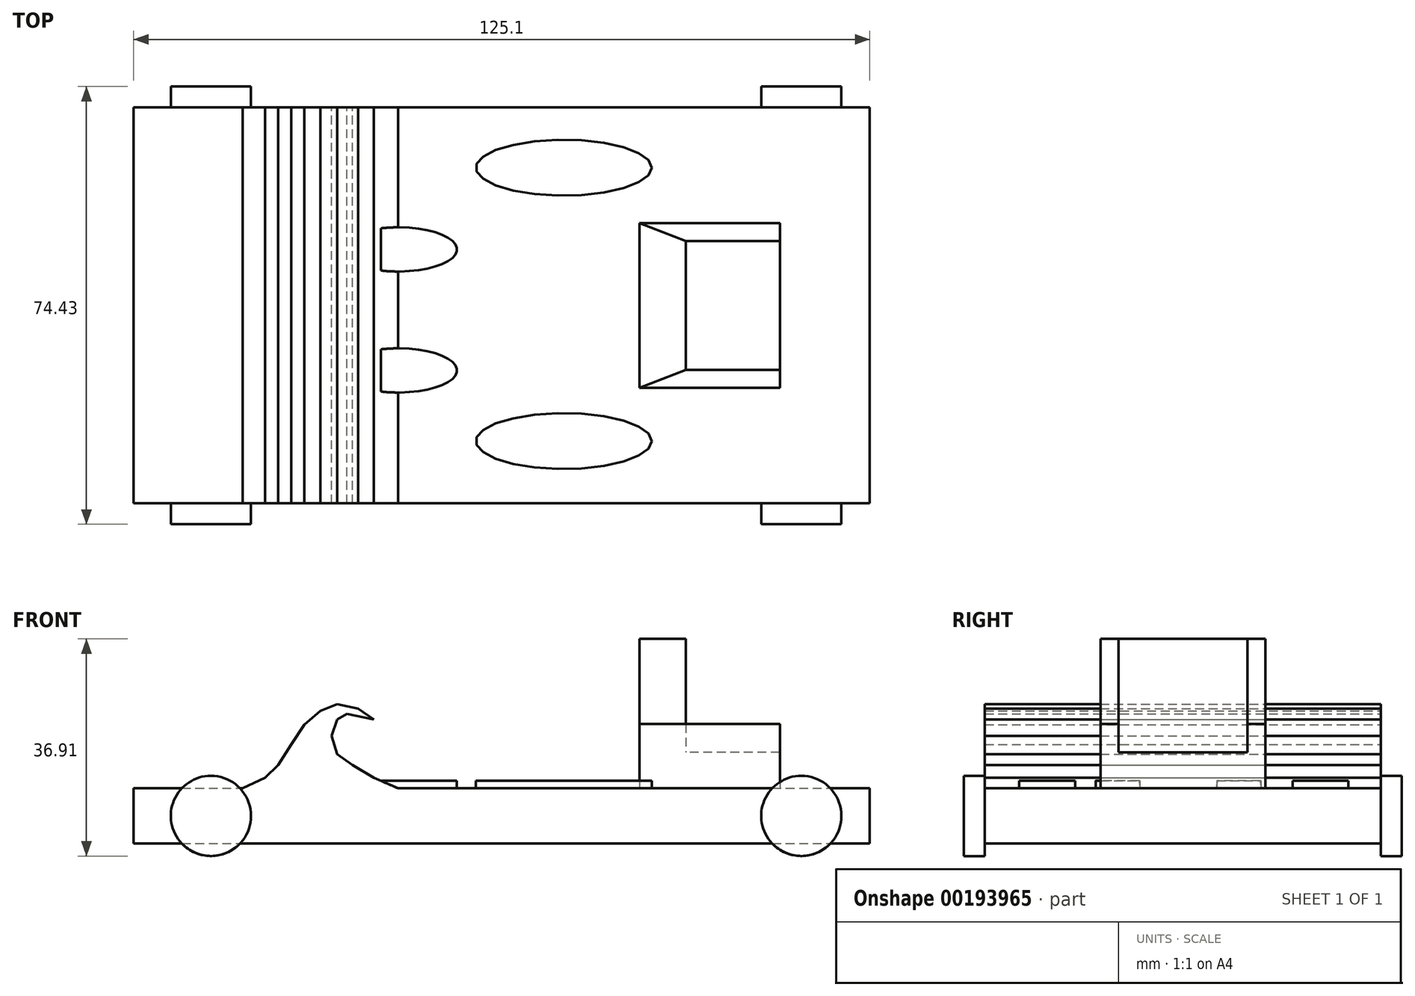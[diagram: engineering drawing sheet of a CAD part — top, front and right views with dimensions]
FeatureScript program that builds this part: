
annotation { "Feature Type Name" : "Feature", "Feature Type Description" : "" }
export const myFeature = defineFeature(function(context is Context, id is Id, definition is map)
    precondition{}
    {
        {
            var Q0;
            Q0=qCreatedBy(makeId("Front.planeOp"),FACE);
            var sketch = newSketch(context, id + "F0", { "sketchPlane" : qUnion([Q0])});
            skLineSegment(sketch, "E0.bottom", {"start": v(-59.68, 0) * mm, "end": v(65.42, 0) * mm});
            skLineSegment(sketch, "E0.top", {"start": v(-59.68, 9.38) * mm, "end": v(65.42, 9.38) * mm});
            skLineSegment(sketch, "E0.left", {"start": v(-59.68, 0) * mm, "end": v(-59.68, 9.38) * mm});
            skLineSegment(sketch, "E0.right", {"start": v(65.42, 0) * mm, "end": v(65.42, 9.38) * mm});
            skLineSegment(sketch, "E1", {"start": v(-41.18, 9.38) * mm, "end": v(-37.35, 11.18) * mm});
            skLineSegment(sketch, "E2", {"start": v(-37.35, 11.18) * mm, "end": v(-35.09, 13.35) * mm});
            skLineSegment(sketch, "E3", {"start": v(-35.09, 13.35) * mm, "end": v(-32.91, 16.83) * mm});
            skLineSegment(sketch, "E4", {"start": v(-32.91, 16.83) * mm, "end": v(-30.65, 20.23) * mm});
            skLineSegment(sketch, "E5", {"start": v(-30.65, 20.23) * mm, "end": v(-27.96, 22.57) * mm});
            skLineSegment(sketch, "E6", {"start": v(-27.96, 22.57) * mm, "end": v(-25.09, 23.7) * mm});
            skLineSegment(sketch, "E7", {"start": v(-25.09, 23.7) * mm, "end": v(-21.52, 22.92) * mm});
            skLineSegment(sketch, "E8", {"start": v(-21.52, 22.92) * mm, "end": v(-18.82, 21.1) * mm});
            skLineSegment(sketch, "E9", {"start": v(-18.82, 21.1) * mm, "end": v(-23.43, 22.05) * mm});
            skLineSegment(sketch, "E10", {"start": v(-23.43, 22.05) * mm, "end": v(-25.09, 21.1) * mm});
            skLineSegment(sketch, "E11", {"start": v(-25.09, 21.1) * mm, "end": v(-26.04, 18.31) * mm});
            skLineSegment(sketch, "E12", {"start": v(-26.04, 18.31) * mm, "end": v(-25.09, 15.18) * mm});
            skLineSegment(sketch, "E13", {"start": v(-25.09, 15.18) * mm, "end": v(-22.48, 13.35) * mm});
            skLineSegment(sketch, "E14", {"start": v(-22.48, 13.35) * mm, "end": v(-18.82, 11.18) * mm});
            skLineSegment(sketch, "E15", {"start": v(-18.82, 11.18) * mm, "end": v(-14.74, 9.38) * mm});
            skSolve(sketch);
        }
        {
            var Q0;
            Q0=makeQuery(id+"F0.imprint","IMPRINT",FACE,{"disambiguationData":[TD([[makeQuery(id+"F0.imprint","IMPRINT",EDGE,{"derivedFrom":sQuery(id+"F0.wireOp",EDGE,"E0.bottom")}),1.0]])]});
            var Q1;
            {var subQ0=sQuery(id+"F0.wireOp",EDGE,"E1");Q1=makeQuery(id+"F0.imprint","IMPRINT",FACE,{"disambiguationData":[TD([[makeQuery(id+"F0.imprint","IMPRINT",EDGE,{"derivedFrom":subQ0}),-1.0]])]});}
            extrude(context, id + "F1", {"entities" : qUnion([Q0, Q1]), "depth" : 67.3 * mm});
        }
        {
            var Q0;
            {var subQ0=sQuery(id+"F0.wireOp",EDGE,"E0.top");Q0=makeQuery(id+"F1.opExtrude","SWEPT_FACE",FACE,{"disambiguationData":[OSD([subQ0]),TDD([makeQuery(id+"F0.imprint","IMPRINT",EDGE,{"disambiguationData":[TD([[makeQuery(id+"F0.imprint","INTERSECT",VERTEX,{"derivedFrom":[subQ0,sQuery(id+"F0.wireOp",EDGE,"E0.right")]}),1.0]])],"derivedFrom":subQ0})])]});}
            var sketch = newSketch(context, id + "F2", { "sketchPlane" : qUnion([Q0])});
            skEllipse(sketch, "E16", {"center": v(13.42, -56.73) * mm, "majorRadius": 14.94 * mm, "minorRadius": 4.74 * mm, "majorAxis": v(1, 0)});
            skEllipse(sketch, "E17.0.1.0", {"center": v(13.42, -41.23) * mm, "majorRadius": 14.94 * mm, "minorRadius": 4.74 * mm, "majorAxis": v(1, 0)});
            skEllipse(sketch, "E17.0.2.0", {"center": v(13.42, -25.74) * mm, "majorRadius": 14.94 * mm, "minorRadius": 4.74 * mm, "majorAxis": v(1, 0)});
            skEllipse(sketch, "E17.0.3.0", {"center": v(13.42, -10.25) * mm, "majorRadius": 14.94 * mm, "minorRadius": 4.74 * mm, "majorAxis": v(1, 0)});
            skLineSegment(sketch, "E17.direction1", {"start": v(13.42, -56.73) * mm, "end": v(24.6, -56.73) * mm, "construction": true});
            skLineSegment(sketch, "E17.direction2", {"start": v(13.42, -56.73) * mm, "end": v(13.42, -41.23) * mm, "construction": true});
            skSolve(sketch);
        }
        {
            var Q0;
            Q0=makeQuery(id+"F2.imprint","IMPRINT",FACE,{"disambiguationData":[TD([[makeQuery(id+"F2.imprint","IMPRINT",EDGE,{"derivedFrom":sQuery(id+"F2.wireOp",EDGE,"E16")}),1.0]])]});
            var Q1;
            Q1=makeQuery(id+"F2.imprint","IMPRINT",FACE,{"disambiguationData":[TD([[makeQuery(id+"F2.imprint","IMPRINT",EDGE,{"derivedFrom":sQuery(id+"F2.wireOp",EDGE,"E17.0.3.0")}),1.0]])]});
            extrude(context, id + "F3", {"entities" : qUnion([Q0, Q1]), "operationType" : NewBodyOperationType.ADD, "depth" : 1.27 * mm});
        }
        {
            var Q0;
            {var subQ0=sQuery(id+"F0.wireOp",EDGE,"E0.top");Q0=makeQuery(id+"F1.opExtrude","SWEPT_FACE",FACE,{"disambiguationData":[OSD([subQ0]),TDD([makeQuery(id+"F0.imprint","IMPRINT",EDGE,{"disambiguationData":[TD([[makeQuery(id+"F0.imprint","INTERSECT",VERTEX,{"derivedFrom":[subQ0,sQuery(id+"F0.wireOp",EDGE,"E0.right")]}),1.0]])],"derivedFrom":subQ0})])]});}
            var sketch = newSketch(context, id + "F4", { "sketchPlane" : qUnion([Q0])});
            skEllipse(sketch, "E18", {"center": v(-14.74, -44.72) * mm, "majorRadius": 10 * mm, "minorRadius": 3.76 * mm, "majorAxis": v(-1, 0)});
            skEllipse(sketch, "E19.0.1.0", {"center": v(-14.74, -24.15) * mm, "majorRadius": 10 * mm, "minorRadius": 3.76 * mm, "majorAxis": v(-1, 0)});
            skLineSegment(sketch, "E19.direction1", {"start": v(-14.74, -44.72) * mm, "end": v(10.66, -44.72) * mm, "construction": true});
            skLineSegment(sketch, "E19.direction2", {"start": v(-14.74, -44.72) * mm, "end": v(-14.74, -24.15) * mm, "construction": true});
            skSolve(sketch);
        }
        {
            var Q0;
            Q0 = qSketchRegion(id + "F4", true);
            extrude(context, id + "F5", {"entities" : qUnion([Q0]), "operationType" : NewBodyOperationType.ADD, "depth" : 1.27 * mm});
        }
        {
            var Q0;
            {var subQ0=sQuery(id+"F0.wireOp",EDGE,"E0.top");Q0=makeQuery(id+"F1.opExtrude","SWEPT_FACE",FACE,{"disambiguationData":[OSD([subQ0]),TDD([makeQuery(id+"F0.imprint","IMPRINT",EDGE,{"disambiguationData":[TD([[makeQuery(id+"F0.imprint","INTERSECT",VERTEX,{"derivedFrom":[subQ0,sQuery(id+"F0.wireOp",EDGE,"E0.right")]}),1.0]])],"derivedFrom":subQ0})])]});}
            var sketch = newSketch(context, id + "F6", { "sketchPlane" : qUnion([Q0])});
            skLineSegment(sketch, "E20.bottom", {"start": v(50.14, -22.7) * mm, "end": v(34.16, -22.7) * mm});
            skLineSegment(sketch, "E20.top", {"start": v(50.14, -44.61) * mm, "end": v(34.16, -44.61) * mm});
            skLineSegment(sketch, "E20.left", {"start": v(50.14, -22.7) * mm, "end": v(50.14, -44.61) * mm});
            skLineSegment(sketch, "E20.right", {"start": v(34.16, -22.7) * mm, "end": v(34.16, -44.61) * mm});
            skPoint(sketch, "E20.middle", {"position": v(42.15, -33.65) * mm});
            skPoint(sketch, "E20.middle.positionSnap0", {"position": v(65.42, -33.65) * mm});
            skPoint(sketch, "E20.centerSnap0", {"position": v(65.42, -33.65) * mm});
            skLineSegment(sketch, "E21", {"start": v(42.15, -33.65) * mm, "end": v(26.31, -33.65) * mm, "construction": true});
            skLineSegment(sketch, "E22", {"start": v(34.16, -44.61) * mm, "end": v(26.31, -47.66) * mm});
            skLineSegment(sketch, "E23", {"start": v(26.31, -47.66) * mm, "end": v(26.31, -33.65) * mm});
            skLineSegment(sketch, "E24.MirrorCS", {"start": v(26.31, -19.65) * mm, "end": v(26.31, -33.65) * mm});
            skLineSegment(sketch, "E25.MirrorCS", {"start": v(34.16, -22.7) * mm, "end": v(26.31, -19.65) * mm});
            skLineSegment(sketch, "E26", {"start": v(26.31, -47.66) * mm, "end": v(50.14, -47.66) * mm});
            skLineSegment(sketch, "E27", {"start": v(50.14, -47.66) * mm, "end": v(50.14, -44.61) * mm});
            skLineSegment(sketch, "E28.MirrorCS", {"start": v(26.31, -19.65) * mm, "end": v(50.14, -19.65) * mm});
            skLineSegment(sketch, "E29.MirrorCS", {"start": v(50.14, -19.65) * mm, "end": v(50.14, -22.7) * mm});
            skSolve(sketch);
        }
        {
            var Q0;
            Q0=makeQuery(id+"F6.imprint","IMPRINT",FACE,{"disambiguationData":[TD([[makeQuery(id+"F6.imprint","IMPRINT",EDGE,{"derivedFrom":sQuery(id+"F6.wireOp",EDGE,"E20.bottom")}),1.0]])]});
            extrude(context, id + "F7", {"entities" : qUnion([Q0]), "operationType" : NewBodyOperationType.ADD, "depth" : 6.1 * mm});
        }
        {
            var Q0;
            Q0=makeQuery(id+"F6.imprint","IMPRINT",FACE,{"disambiguationData":[TD([[makeQuery(id+"F6.imprint","IMPRINT",EDGE,{"derivedFrom":sQuery(id+"F6.wireOp",EDGE,"E20.top")}),1.0]])]});
            var Q1;
            Q1=makeQuery(id+"F6.imprint","IMPRINT",FACE,{"disambiguationData":[TD([[makeQuery(id+"F6.imprint","IMPRINT",EDGE,{"derivedFrom":sQuery(id+"F6.wireOp",EDGE,"E20.bottom")}),-1.0]])]});
            extrude(context, id + "F8", {"entities" : qUnion([Q0, Q1]), "operationType" : NewBodyOperationType.ADD, "depth" : 10.92 * mm});
        }
        {
            var Q0;
            Q0=makeQuery(id+"F6.imprint","IMPRINT",FACE,{"disambiguationData":[TD([[makeQuery(id+"F6.imprint","IMPRINT",EDGE,{"derivedFrom":sQuery(id+"F6.wireOp",EDGE,"E20.right")}),-1.0]])]});
            extrude(context, id + "F9", {"entities" : qUnion([Q0]), "operationType" : NewBodyOperationType.ADD, "depth" : 25.4 * mm});
        }
        {
            var Q0;
            Q0=makeQuery(id+"F1.opExtrude","CAP_FACE",FACE,{"disambiguationData":[OSD([sQuery(id+"F0.wireOp",EDGE,"E0.bottom"),sQuery(id+"F0.wireOp",EDGE,"E0.top"),sQuery(id+"F0.wireOp",EDGE,"E0.left"),sQuery(id+"F0.wireOp",EDGE,"E0.right"),sQuery(id+"F0.wireOp",EDGE,"E1"),sQuery(id+"F0.wireOp",EDGE,"E2"),sQuery(id+"F0.wireOp",EDGE,"E3"),sQuery(id+"F0.wireOp",EDGE,"E4"),sQuery(id+"F0.wireOp",EDGE,"E5"),sQuery(id+"F0.wireOp",EDGE,"E6"),sQuery(id+"F0.wireOp",EDGE,"E7"),sQuery(id+"F0.wireOp",EDGE,"E8"),sQuery(id+"F0.wireOp",EDGE,"E9"),sQuery(id+"F0.wireOp",EDGE,"E10"),sQuery(id+"F0.wireOp",EDGE,"E11"),sQuery(id+"F0.wireOp",EDGE,"E12"),sQuery(id+"F0.wireOp",EDGE,"E13"),sQuery(id+"F0.wireOp",EDGE,"E14"),sQuery(id+"F0.wireOp",EDGE,"E15")])],"isStart":true});
            var sketch = newSketch(context, id + "F10", { "sketchPlane" : qUnion([Q0])});
            skCircle(sketch, "E30", {"center": v(-53.79, 4.7) * mm, "radius": 6.82 * mm});
            skPoint(sketch, "E30.centerSnap0", {"position": v(-65.42, 4.7) * mm});
            skCircle(sketch, "E31.1.0.0", {"center": v(46.54, 4.7) * mm, "radius": 6.82 * mm});
            skLineSegment(sketch, "E31.direction1", {"start": v(-53.79, 4.7) * mm, "end": v(46.54, 4.7) * mm, "construction": true});
            skSolve(sketch);
        }
        {
            var Q0;
            {var subQ0=sQuery(id+"F0.wireOp",EDGE,"E0.top");Q0=makeQuery(id+"F1.opExtrude","SWEPT_FACE",FACE,{"disambiguationData":[OSD([subQ0]),TDD([makeQuery(id+"F0.imprint","IMPRINT",EDGE,{"disambiguationData":[TD([[makeQuery(id+"F0.imprint","INTERSECT",VERTEX,{"derivedFrom":[subQ0,sQuery(id+"F0.wireOp",EDGE,"E0.right")]}),1.0]])],"derivedFrom":subQ0})])]});}
            var sketch = newSketch(context, id + "F11", { "sketchPlane" : qUnion([Q0])});
            skLineSegment(sketch, "E32.bottom", {"start": v(50.14, -33.65) * mm, "end": v(80.7, -33.65) * mm});
            skLineSegment(sketch, "E32.top", {"start": v(50.14, -42.65) * mm, "end": v(80.7, -42.65) * mm});
            skLineSegment(sketch, "E32.left", {"start": v(50.14, -33.65) * mm, "end": v(50.14, -42.65) * mm});
            skLineSegment(sketch, "E32.right", {"start": v(80.7, -33.65) * mm, "end": v(80.7, -42.65) * mm});
            skPoint(sketch, "E32.middle", {"position": v(65.42, -38.15) * mm});
            skSolve(sketch);
        }
        {
            var Q0;
            {var subQ0=sQuery(id+"F10.wireOp",EDGE,"E30");var subQ4=makeQuery(id+"F1.opExtrude","CAP_EDGE",EDGE,{"disambiguationData":[OSD([sQuery(id+"F0.wireOp",EDGE,"E0.bottom")])],"isStart":true});var subQ5=makeQuery(id+"F10.imprint","INTERSECT",VERTEX,{"disambiguationData":[OD(0.0)],"derivedFrom":[subQ4,subQ0]});Q0=makeQuery(id+"F10.imprint","IMPRINT",FACE,{"disambiguationData":[TD([[makeQuery(id+"F10.imprint","IMPRINT",EDGE,{"disambiguationData":[TD([[subQ5,1.0]])],"derivedFrom":subQ4}),-1.0]])]});}
            var Q1;
            {var subQ0=sQuery(id+"F10.wireOp",EDGE,"E30");var subQ1=sQuery(id+"F0.wireOp",EDGE,"E0.top");var subQ2=makeQuery(id+"F1.opExtrude","CAP_EDGE",EDGE,{"disambiguationData":[OSD([subQ1]),TDD([makeQuery(id+"F0.imprint","IMPRINT",EDGE,{"disambiguationData":[TD([[makeQuery(id+"F0.imprint","INTERSECT",VERTEX,{"derivedFrom":[subQ1,sQuery(id+"F0.wireOp",EDGE,"E0.right")]}),1.0]])],"derivedFrom":subQ1})])],"isStart":true});var subQ3=makeQuery(id+"F10.imprint","INTERSECT",VERTEX,{"disambiguationData":[OD(0.0)],"derivedFrom":[subQ2,subQ0]});Q1=makeQuery(id+"F10.imprint","IMPRINT",FACE,{"disambiguationData":[TD([[makeQuery(id+"F10.imprint","IMPRINT",EDGE,{"disambiguationData":[TD([[subQ3,1.0]])],"derivedFrom":subQ0}),1.0]])]});}
            var Q2;
            {var subQ0=sQuery(id+"F10.wireOp",EDGE,"E30");var subQ1=makeQuery(id+"F1.opExtrude","CAP_EDGE",EDGE,{"disambiguationData":[OSD([sQuery(id+"F0.wireOp",EDGE,"E0.bottom")])],"isStart":true});var subQ2=makeQuery(id+"F10.imprint","INTERSECT",VERTEX,{"disambiguationData":[OD(0.0)],"derivedFrom":[subQ1,subQ0]});Q2=makeQuery(id+"F10.imprint","IMPRINT",FACE,{"disambiguationData":[TD([[makeQuery(id+"F10.imprint","IMPRINT",EDGE,{"disambiguationData":[TD([[subQ2,-1.0]])],"derivedFrom":subQ0}),1.0]])]});}
            var Q3;
            {var subQ0=sQuery(id+"F10.wireOp",EDGE,"E31.1.0.0");var subQ1=sQuery(id+"F0.wireOp",EDGE,"E0.top");var subQ2=makeQuery(id+"F1.opExtrude","CAP_EDGE",EDGE,{"disambiguationData":[OSD([subQ1]),TDD([makeQuery(id+"F0.imprint","IMPRINT",EDGE,{"disambiguationData":[TD([[makeQuery(id+"F0.imprint","INTERSECT",VERTEX,{"derivedFrom":[subQ1,sQuery(id+"F0.wireOp",EDGE,"E0.left")]}),-1.0]])],"derivedFrom":subQ1})])],"isStart":true});var subQ3=makeQuery(id+"F10.imprint","INTERSECT",VERTEX,{"disambiguationData":[OD(0.0)],"derivedFrom":[subQ2,subQ0]});Q3=makeQuery(id+"F10.imprint","IMPRINT",FACE,{"disambiguationData":[TD([[makeQuery(id+"F10.imprint","IMPRINT",EDGE,{"disambiguationData":[TD([[subQ3,1.0]])],"derivedFrom":subQ0}),1.0]])]});}
            var Q4;
            {var subQ0=sQuery(id+"F10.wireOp",EDGE,"E31.1.0.0");var subQ4=makeQuery(id+"F1.opExtrude","CAP_EDGE",EDGE,{"disambiguationData":[OSD([sQuery(id+"F0.wireOp",EDGE,"E0.bottom")])],"isStart":true});var subQ5=makeQuery(id+"F10.imprint","INTERSECT",VERTEX,{"disambiguationData":[OD(0.0)],"derivedFrom":[subQ4,subQ0]});Q4=makeQuery(id+"F10.imprint","IMPRINT",FACE,{"disambiguationData":[TD([[makeQuery(id+"F10.imprint","IMPRINT",EDGE,{"disambiguationData":[TD([[subQ5,1.0]])],"derivedFrom":subQ4}),-1.0]])]});}
            var Q5;
            {var subQ0=sQuery(id+"F10.wireOp",EDGE,"E31.1.0.0");var subQ1=makeQuery(id+"F1.opExtrude","CAP_EDGE",EDGE,{"disambiguationData":[OSD([sQuery(id+"F0.wireOp",EDGE,"E0.bottom")])],"isStart":true});var subQ2=makeQuery(id+"F10.imprint","INTERSECT",VERTEX,{"disambiguationData":[OD(0.0)],"derivedFrom":[subQ1,subQ0]});Q5=makeQuery(id+"F10.imprint","IMPRINT",FACE,{"disambiguationData":[TD([[makeQuery(id+"F10.imprint","IMPRINT",EDGE,{"disambiguationData":[TD([[subQ2,-1.0]])],"derivedFrom":subQ0}),1.0]])]});}
            extrude(context, id + "F12", {"entities" : qUnion([Q0, Q1, Q2, Q3, Q4, Q5]), "depth" : 3.56 * mm});
        }
        {
            var Q0;
            {var subQ0=sQuery(id+"F11.wireOp",EDGE,"E32.left");Q0=makeQuery(id+"F11.imprint","IMPRINT",FACE,{"disambiguationData":[TD([[makeQuery(id+"F11.imprint","IMPRINT",EDGE,{"derivedFrom":subQ0}),1.0]])]});}
            extrude(context, id + "F13", {"entities" : qUnion([Q0]), "operationType" : NewBodyOperationType.ADD, "depth" : 25.4 * mm});
        }
        {
            var Q0;
            Q0=makeQuery(id+"F12.opExtrude","SWEPT_BODY",BODY,{"disambiguationData":[OSD([sQuery(id+"F10.wireOp",EDGE,"E30")])]});
            var Q1;
            Q1=makeQuery(id+"F12.opExtrude","SWEPT_BODY",BODY,{"disambiguationData":[OSD([sQuery(id+"F10.wireOp",EDGE,"E31.1.0.0")])]});
            var Q2;
            Q2=makeQuery(id+"F13.opExtrude","SWEPT_FACE",FACE,{"disambiguationData":[OSD([sQuery(id+"F11.wireOp",EDGE,"E32.bottom")])]});
            mirror(context, id + "F14", {"operationType" : NewBodyOperationType.ADD, "entities" : qUnion([Q0, Q1]), "mirrorPlane" : qUnion([Q2])});
        }
        {
            var Q0;
            Q0=makeQuery(id+"F13.opExtrude","CAP_FACE",FACE,{"disambiguationData":[OSD([sQuery(id+"F0.wireOp",EDGE,"E0.top"),sQuery(id+"F0.wireOp",EDGE,"E0.right"),sQuery(id+"F11.wireOp",EDGE,"E32.bottom"),sQuery(id+"F11.wireOp",EDGE,"E32.top"),sQuery(id+"F11.wireOp",EDGE,"E32.left")])],"isStart":false});
            extrude(context, id + "F15", {"entities" : qUnion([Q0]), "operationType" : NewBodyOperationType.REMOVE, "oppositeDirection" : true, "depth" : 25.4 * mm});
        }
    });
